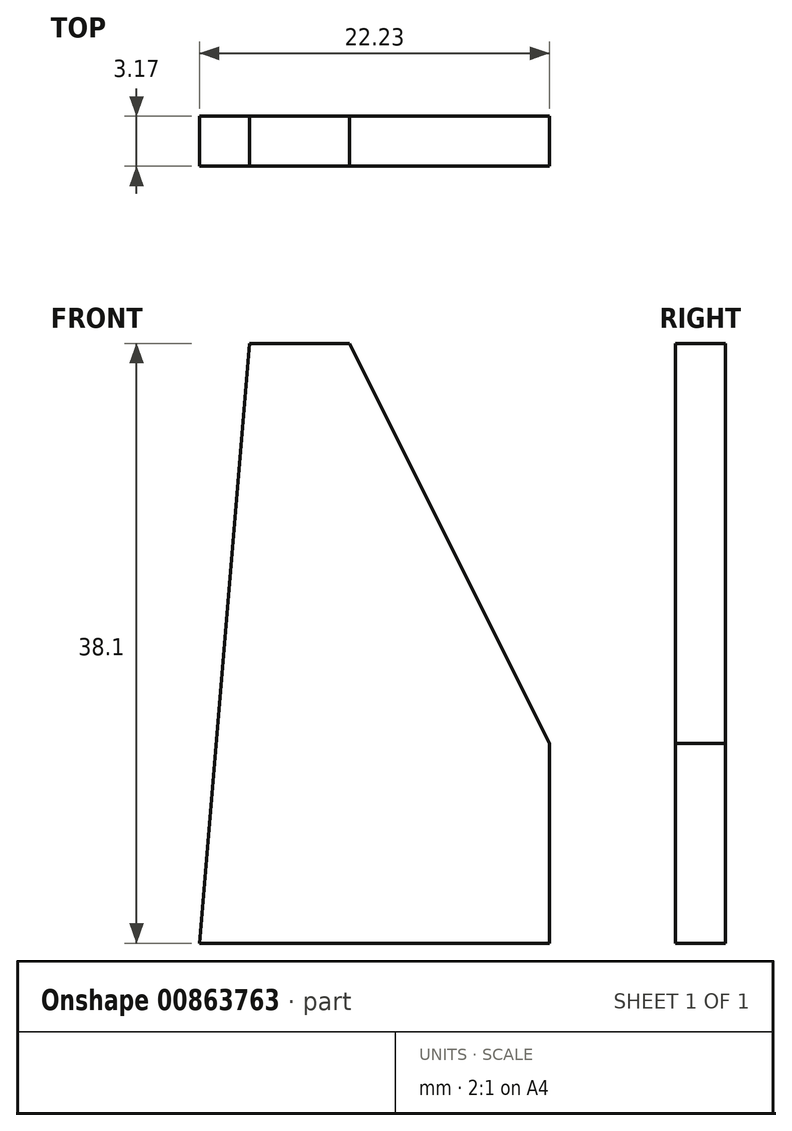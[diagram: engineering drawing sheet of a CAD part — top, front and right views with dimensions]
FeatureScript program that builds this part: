
annotation { "Feature Type Name" : "Feature", "Feature Type Description" : "" }
export const myFeature = defineFeature(function(context is Context, id is Id, definition is map)
    precondition{}
    {
        {
            var Q0;
            Q0=qCreatedBy(makeId("Front.planeOp"),FACE);
            var sketch = newSketch(context, id + "F0", { "sketchPlane" : qUnion([Q0])});
            skLineSegment(sketch, "E0.bottom", {"start": v(17.75, -17.47) * mm, "end": v(-4.48, -17.47) * mm});
            skLineSegment(sketch, "E1", {"start": v(17.75, -17.47) * mm, "end": v(17.75, -4.77) * mm});
            skLineSegment(sketch, "E2", {"start": v(-1.3, 20.63) * mm, "end": v(5.05, 20.63) * mm});
            skLineSegment(sketch, "E3", {"start": v(5.05, 20.63) * mm, "end": v(17.75, -4.77) * mm});
            skPoint(sketch, "E4", {"position": v(-1.3, 20.63) * mm});
            skLineSegment(sketch, "E5", {"start": v(-1.3, 20.63) * mm, "end": v(-4.48, -17.47) * mm});
            skPoint(sketch, "E0.right.end.orphan", {"position": v(-4.48, 20.63) * mm});
            skSolve(sketch);
        }
        {
            var Q0;
            Q0=makeQuery(id+"F0.imprint","IMPRINT",FACE,{"disambiguationData":[TD([[makeQuery(id+"F0.imprint","IMPRINT",EDGE,{"derivedFrom":sQuery(id+"F0.wireOp",EDGE,"E0.bottom")}),-1.0]])]});
            extrude(context, id + "F1", {"entities" : qUnion([Q0]), "depth" : 3.17 * mm, "offsetDistance" : 25.4 * mm});
        }
    });
